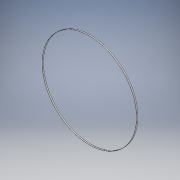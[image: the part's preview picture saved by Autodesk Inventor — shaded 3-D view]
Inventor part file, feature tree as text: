
AUTODESK INVENTOR PART (.ipt)
format: ipt  version: 2019 (Build 230136000, 136)  size: 104,448 bytes
history: native  units: mm
features: extrude x2, sketch x2
ambient origin geometry x8: Origin, YZ Plane, XZ Plane, XY Plane, X Axis, Y Axis, Z Axis, Center Point
bodies: Solid1 (feature_tree)
feature tree (4):
  extrude  "Extrusion1"  Depth=1.365mm TaperAngle=0.0deg
  extrude  "Extrusion2"  Depth=1.365mm TaperAngle=0.0deg
  sketch  "Sketch1"  dims[d0=99.6mm d1=1.365mm d2=0.0mm]
  sketch  "Sketch2"  dims[d3=99.3mm d4=1.365mm d5=0.0mm]
